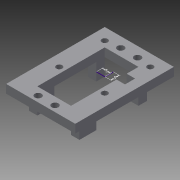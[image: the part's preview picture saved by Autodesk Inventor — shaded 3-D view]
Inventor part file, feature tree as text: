
AUTODESK INVENTOR PART (.ipt)
format: ipt  version: 2015 (Build 190159000, 159)  size: 198,144 bytes
history: native  units: mm
features: sketch x5, extrude x4, pattern_circular x1, pattern_linear x1
ambient origin geometry x8: Origin, YZ Plane, XZ Plane, XY Plane, X Axis, Y Axis, Z Axis, Center Point
bodies: Solid1 (feature_tree)
feature tree (11):
  extrude  "Extrusion1"  Depth=17.5mm
  extrude  "Extrusion2"  Depth=35.0mm
  pattern_circular  "Circular Pattern1"  Count=4 Angle=360.0deg
  sketch  "Sketch3"  dims[d4=4.0mm]
  pattern_linear  "Rectangular Pattern1"  Spacing1=10.0mm  [1 undecoded]
  extrude  "Extrusion3"  Depth=20.0mm
  extrude  "Extrusion4"  Depth=40.0mm
  sketch  "Sketch1"  dims[d0=17.5mm d1=17.5mm]
  sketch  "Sketch2"  dims[d2=35.0mm d3=4.0mm]
  sketch  "Sketch4"  dims[d5=3.5mm d6=40.0mm d8=360.0deg]
  sketch  "Sketch5"  dims[d10=10.0mm d11=10.0mm d12=20.0mm d13=40.0mm d14=20.0mm d15=35.0mm d16=7.0mm d17=5.0mm d18=6.0mm d19=3.0mm d20=38.0mm d21=58.5mm d22=41.0mm d23=5.0mm d24=0.0mm d25=3.0mm d26=3.0mm d27=60.0deg d28=2.5mm d29=0.0mm d30=60.0mm d31=360.0deg d33=5.0mm d34=5.0mm d35=20.0mm d37=27.0mm d38=20.0mm d40=27.0mm d41=4.5mm d42=3.0mm d43=6.0mm d44=2.0mm d45=2.0mm d46=4.0mm d47=4.0mm d48=20.0mm d49=2.5mm d50=0.0mm d51=5.0mm d52=10.0mm d53=5.0mm d54=10.0mm d55=5.0mm d56=5.0mm d57=5.0mm d58=5.0mm d59=10.0mm d60=0.0mm]
note: 1 required parameter value undecoded (feature->parameter linkage not recoverable at this tier; creation-order binding heuristic only, values carry confidence <= 0.55)
